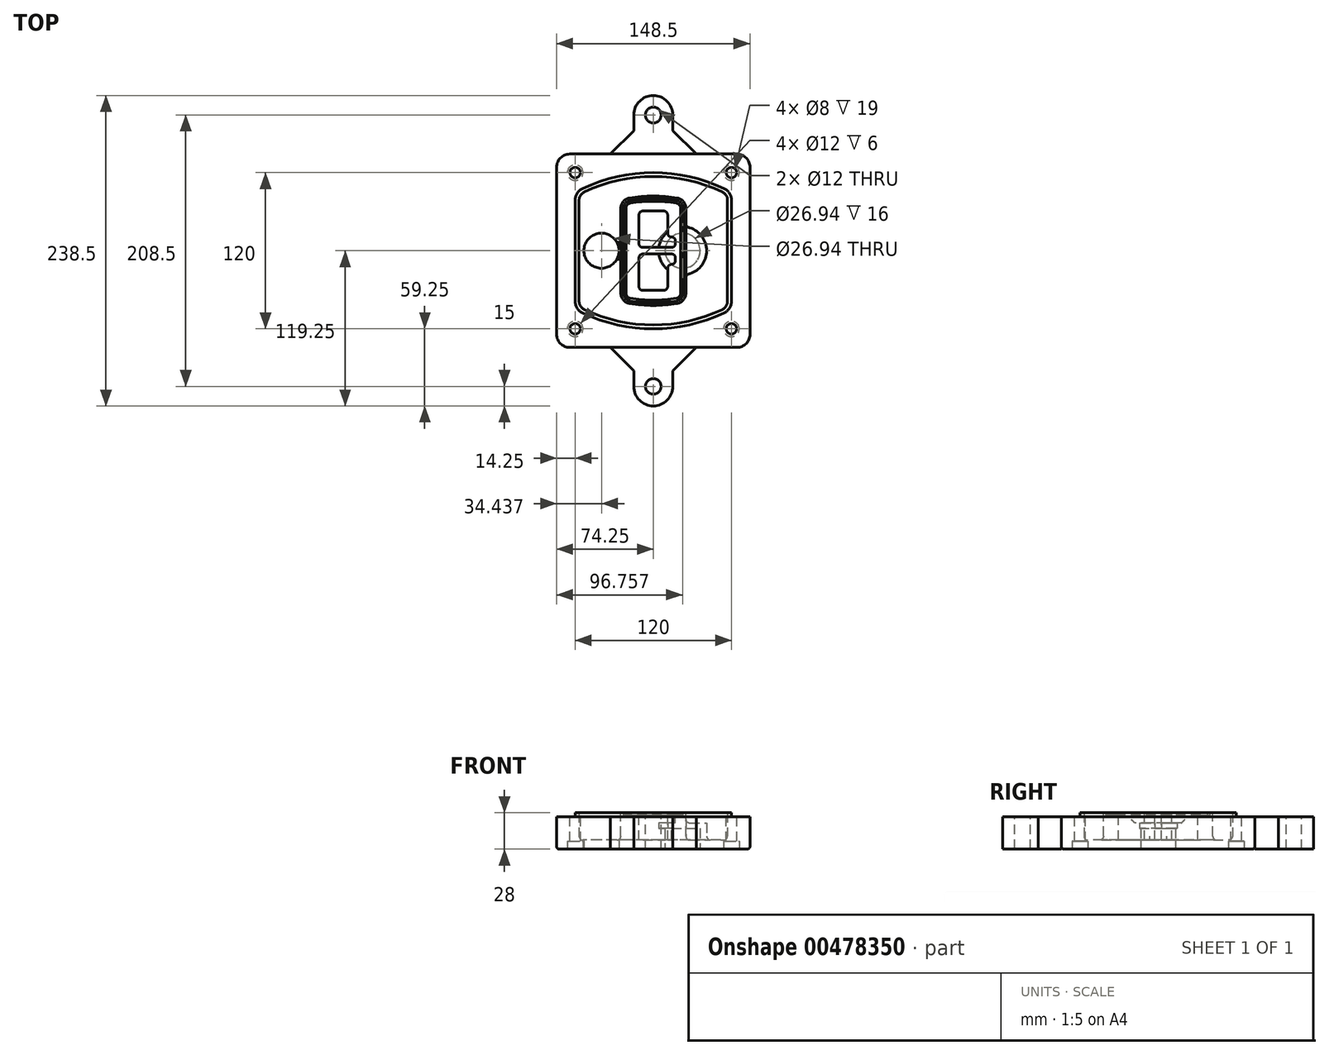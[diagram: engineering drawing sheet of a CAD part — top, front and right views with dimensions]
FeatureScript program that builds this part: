
annotation { "Feature Type Name" : "Feature", "Feature Type Description" : "" }
export const myFeature = defineFeature(function(context is Context, id is Id, definition is map)
    precondition{}
    {
        {
            var Q0;
            Q0=qCreatedBy(makeId("Top.planeOp"),FACE);
            var sketch = newSketch(context, id + "F0", { "sketchPlane" : qUnion([Q0])});
            skPoint(sketch, "E0.rect.middle", {"position": v(0, 0) * mm});
            skLineSegment(sketch, "E1.bottom", {"start": v(-64.25, -74.25) * mm, "end": v(64.25, -74.25) * mm});
            skLineSegment(sketch, "E1.top", {"start": v(-64.25, 74.25) * mm, "end": v(64.25, 74.25) * mm});
            skLineSegment(sketch, "E1.left", {"start": v(-74.25, -64.25) * mm, "end": v(-74.25, 64.25) * mm});
            skLineSegment(sketch, "E1.right", {"start": v(74.25, -64.25) * mm, "end": v(74.25, 64.25) * mm});
            skLineSegment(sketch, "E2", {"start": v(-74.25, 74.25) * mm, "end": v(74.25, -74.25) * mm, "construction": true});
            skLineSegment(sketch, "E3", {"start": v(74.25, 74.25) * mm, "end": v(-74.25, -74.25) * mm, "construction": true});
            skCircle(sketch, "E4", {"center": v(-60, 60) * mm, "radius": 4 * mm});
            skCircle(sketch, "E5", {"center": v(60, 60) * mm, "radius": 4 * mm});
            skCircle(sketch, "E6", {"center": v(60, -60) * mm, "radius": 4 * mm});
            skCircle(sketch, "E7", {"center": v(-60, -60) * mm, "radius": 4 * mm});
            skLineSegment(sketch, "E8", {"start": v(-60, 60) * mm, "end": v(60, 60) * mm, "construction": true});
            skLineSegment(sketch, "E9", {"start": v(60, 60) * mm, "end": v(60, -60) * mm, "construction": true});
            skLineSegment(sketch, "E10", {"start": v(60, -60) * mm, "end": v(-60, -60) * mm, "construction": true});
            skLineSegment(sketch, "E11", {"start": v(-60, -60) * mm, "end": v(-60, 60) * mm, "construction": true});
            skLineSegment(sketch, "E12", {"start": v(-60, 38.83) * mm, "end": v(-60, -38.83) * mm});
            skLineSegment(sketch, "E13", {"start": v(60, 38.83) * mm, "end": v(60, -38.83) * mm});
            skArc(sketch, "E14", {"start": v(54.26, 47.88) * mm, "mid": v(0, 60) * mm, "end": v(-54.26, 47.88) * mm});
            skArc(sketch, "E15", {"start": v(-54.26, -47.88) * mm, "mid": v(0, -60) * mm, "end": v(54.26, -47.88) * mm});
            skLineSegment(sketch, "E16", {"start": v(-60, 0) * mm, "end": v(60, 0) * mm, "construction": true});
            skPoint(sketch, "E17.visualSharp", {"position": v(-60, -45) * mm});
            skArc(sketch, "E17.filletArc", {"start": v(-60, -38.83) * mm, "mid": v(-58.44, -44.2) * mm, "end": v(-54.26, -47.88) * mm});
            skPoint(sketch, "E18.visualSharp", {"position": v(-60, 45) * mm});
            skArc(sketch, "E18.filletArc", {"start": v(-54.26, 47.88) * mm, "mid": v(-58.44, 44.2) * mm, "end": v(-60, 38.83) * mm});
            skPoint(sketch, "E19.visualSharp", {"position": v(60, 45) * mm});
            skArc(sketch, "E19.filletArc", {"start": v(60, 38.83) * mm, "mid": v(58.44, 44.2) * mm, "end": v(54.26, 47.88) * mm});
            skPoint(sketch, "E20.visualSharp", {"position": v(60, -45) * mm});
            skArc(sketch, "E20.filletArc", {"start": v(54.26, -47.88) * mm, "mid": v(58.44, -44.2) * mm, "end": v(60, -38.83) * mm});
            skPoint(sketch, "E21.visualSharp", {"position": v(-74.25, 74.25) * mm});
            skArc(sketch, "E21.filletArc", {"start": v(-64.25, 74.25) * mm, "mid": v(-71.32, 71.32) * mm, "end": v(-74.25, 64.25) * mm});
            skPoint(sketch, "E22.visualSharp", {"position": v(74.25, 74.25) * mm});
            skArc(sketch, "E22.filletArc", {"start": v(74.25, 64.25) * mm, "mid": v(71.32, 71.32) * mm, "end": v(64.25, 74.25) * mm});
            skPoint(sketch, "E23.visualSharp", {"position": v(74.25, -74.25) * mm});
            skArc(sketch, "E23.filletArc", {"start": v(64.25, -74.25) * mm, "mid": v(71.32, -71.32) * mm, "end": v(74.25, -64.25) * mm});
            skPoint(sketch, "E24.visualSharp", {"position": v(-74.25, -74.25) * mm});
            skArc(sketch, "E24.filletArc", {"start": v(-74.25, -64.25) * mm, "mid": v(-71.32, -71.32) * mm, "end": v(-64.25, -74.25) * mm});
            skArc(sketch, "E25.0", {"start": v(57, 38.83) * mm, "mid": v(55.9, 42.58) * mm, "end": v(52.98, 45.17) * mm});
            skLineSegment(sketch, "E25.1", {"start": v(57, 38.83) * mm, "end": v(57, -38.83) * mm});
            skArc(sketch, "E25.2", {"start": v(52.98, -45.17) * mm, "mid": v(55.9, -42.58) * mm, "end": v(57, -38.83) * mm});
            skArc(sketch, "E25.3", {"start": v(-52.98, -45.17) * mm, "mid": v(0, -57) * mm, "end": v(52.98, -45.17) * mm});
            skArc(sketch, "E25.4", {"start": v(-57, -38.83) * mm, "mid": v(-55.9, -42.58) * mm, "end": v(-52.98, -45.17) * mm});
            skArc(sketch, "E25.5", {"start": v(52.98, 45.17) * mm, "mid": v(0, 57) * mm, "end": v(-52.98, 45.17) * mm});
            skLineSegment(sketch, "E25.6", {"start": v(-57, 38.83) * mm, "end": v(-57, -38.83) * mm});
            skArc(sketch, "E25.7", {"start": v(-52.98, 45.17) * mm, "mid": v(-55.9, 42.58) * mm, "end": v(-57, 38.83) * mm});
            skArc(sketch, "E26.0", {"start": v(-55.96, 51.5) * mm, "mid": v(-61.82, 46.33) * mm, "end": v(-64, 38.83) * mm});
            skArc(sketch, "E26.1", {"start": v(55.96, 51.5) * mm, "mid": v(0, 64) * mm, "end": v(-55.96, 51.5) * mm});
            skArc(sketch, "E26.2", {"start": v(64, 38.83) * mm, "mid": v(61.82, 46.33) * mm, "end": v(55.96, 51.5) * mm});
            skLineSegment(sketch, "E26.3", {"start": v(64, 38.83) * mm, "end": v(64, -38.83) * mm});
            skArc(sketch, "E26.4", {"start": v(55.96, -51.5) * mm, "mid": v(61.82, -46.33) * mm, "end": v(64, -38.83) * mm});
            skLineSegment(sketch, "E26.5", {"start": v(-64, 38.83) * mm, "end": v(-64, -38.83) * mm});
            skArc(sketch, "E26.6", {"start": v(-55.96, -51.5) * mm, "mid": v(0, -64) * mm, "end": v(55.96, -51.5) * mm});
            skArc(sketch, "E26.7", {"start": v(-64, -38.83) * mm, "mid": v(-61.82, -46.33) * mm, "end": v(-55.96, -51.5) * mm});
            skSolve(sketch);
        }
        {
            var Q0;
            Q0=makeQuery(id+"F0.imprint","IMPRINT",FACE,{"disambiguationData":[TD([[makeQuery(id+"F0.imprint","IMPRINT",EDGE,{"derivedFrom":sQuery(id+"F0.wireOp",EDGE,"E1.bottom")}),1.0]])]});
            var Q1;
            Q1=makeQuery(id+"F0.imprint","IMPRINT",FACE,{"disambiguationData":[TD([[makeQuery(id+"F0.imprint","IMPRINT",EDGE,{"derivedFrom":sQuery(id+"F0.wireOp",EDGE,"E12")}),1.0]])]});
            var Q2;
            Q2=makeQuery(id+"F0.imprint","IMPRINT",FACE,{"disambiguationData":[TD([[makeQuery(id+"F0.imprint","IMPRINT",EDGE,{"derivedFrom":sQuery(id+"F0.wireOp",EDGE,"E25.0")}),1.0]])]});
            var Q3;
            Q3=makeQuery(id+"F0.imprint","IMPRINT",FACE,{"disambiguationData":[TD([[makeQuery(id+"F0.imprint","IMPRINT",EDGE,{"derivedFrom":sQuery(id+"F0.wireOp",EDGE,"E12")}),-1.0]])]});
            extrude(context, id + "F1", {"entities" : qUnion([Q0, Q1, Q2, Q3]), "oppositeDirection" : true, "depth" : 25 * mm});
        }
        {
            var Q0;
            Q0=makeQuery(id+"F0.imprint","IMPRINT",FACE,{"disambiguationData":[TD([[makeQuery(id+"F0.imprint","IMPRINT",EDGE,{"derivedFrom":sQuery(id+"F0.wireOp",EDGE,"E12")}),1.0]])]});
            extrude(context, id + "F2", {"entities" : qUnion([Q0]), "operationType" : NewBodyOperationType.ADD, "depth" : 3 * mm});
        }
        {
            var Q0;
            Q0=makeQuery(id+"F0.imprint","IMPRINT",FACE,{"disambiguationData":[TD([[makeQuery(id+"F0.imprint","IMPRINT",EDGE,{"derivedFrom":sQuery(id+"F0.wireOp",EDGE,"E25.0")}),1.0]])]});
            extrude(context, id + "F3", {"entities" : qUnion([Q0]), "operationType" : NewBodyOperationType.REMOVE, "oppositeDirection" : true, "depth" : 18 * mm});
        }
        {
            var Q0;
            Q0=makeQuery(id+"F2.opExtrude","CAP_FACE",FACE,{"disambiguationData":[OSD([sQuery(id+"F0.wireOp",EDGE,"E12"),sQuery(id+"F0.wireOp",EDGE,"E13"),sQuery(id+"F0.wireOp",EDGE,"E14"),sQuery(id+"F0.wireOp",EDGE,"E15"),sQuery(id+"F0.wireOp",EDGE,"E17.filletArc"),sQuery(id+"F0.wireOp",EDGE,"E18.filletArc"),sQuery(id+"F0.wireOp",EDGE,"E19.filletArc"),sQuery(id+"F0.wireOp",EDGE,"E20.filletArc"),sQuery(id+"F0.wireOp",EDGE,"E25.0"),sQuery(id+"F0.wireOp",EDGE,"E25.1"),sQuery(id+"F0.wireOp",EDGE,"E25.2"),sQuery(id+"F0.wireOp",EDGE,"E25.3"),sQuery(id+"F0.wireOp",EDGE,"E25.4"),sQuery(id+"F0.wireOp",EDGE,"E25.5"),sQuery(id+"F0.wireOp",EDGE,"E25.6"),sQuery(id+"F0.wireOp",EDGE,"E25.7")])],"isStart":false});
            var sketch = newSketch(context, id + "F4", { "sketchPlane" : qUnion([Q0])});
            skArc(sketch, "E27.0", {"start": v(-18.34, -40.45) * mm, "mid": v(0, -42) * mm, "end": v(18.34, -40.45) * mm});
            skArc(sketch, "E28.0", {"start": v(18.34, 40.45) * mm, "mid": v(0, 42) * mm, "end": v(-18.34, 40.45) * mm});
            skLineSegment(sketch, "E29", {"start": v(-25, 32.57) * mm, "end": v(-25, -32.57) * mm});
            skLineSegment(sketch, "E30", {"start": v(25, 32.57) * mm, "end": v(25, -32.57) * mm});
            skLineSegment(sketch, "E31", {"start": v(-25, 39.1) * mm, "end": v(25, 39.1) * mm, "construction": true});
            skLineSegment(sketch, "E32", {"start": v(-25, -39.1) * mm, "end": v(25, -39.1) * mm, "construction": true});
            skPoint(sketch, "E33.visualSharp", {"position": v(-25, 39.1) * mm});
            skArc(sketch, "E33.filletArc", {"start": v(-18.34, 40.45) * mm, "mid": v(-23.11, 37.73) * mm, "end": v(-25, 32.57) * mm});
            skPoint(sketch, "E34.visualSharp", {"position": v(25, 39.1) * mm});
            skArc(sketch, "E34.filletArc", {"start": v(25, 32.57) * mm, "mid": v(23.11, 37.73) * mm, "end": v(18.34, 40.45) * mm});
            skPoint(sketch, "E35.visualSharp", {"position": v(25, -39.1) * mm});
            skArc(sketch, "E35.filletArc", {"start": v(18.34, -40.45) * mm, "mid": v(23.11, -37.73) * mm, "end": v(25, -32.57) * mm});
            skPoint(sketch, "E36.visualSharp", {"position": v(-25, -39.1) * mm});
            skArc(sketch, "E36.filletArc", {"start": v(-25, -32.57) * mm, "mid": v(-23.11, -37.73) * mm, "end": v(-18.34, -40.45) * mm});
            skArc(sketch, "E37.0", {"start": v(52.98, 45.17) * mm, "mid": v(0, 57) * mm, "end": v(-52.98, 45.17) * mm});
            skArc(sketch, "E37.1", {"start": v(-52.98, 45.17) * mm, "mid": v(-55.9, 42.58) * mm, "end": v(-57, 38.83) * mm});
            skLineSegment(sketch, "E37.2", {"start": v(-57, 38.83) * mm, "end": v(-57, -38.83) * mm});
            skArc(sketch, "E37.3", {"start": v(-57, -38.83) * mm, "mid": v(-55.9, -42.58) * mm, "end": v(-52.98, -45.17) * mm});
            skArc(sketch, "E37.4", {"start": v(-52.98, -45.17) * mm, "mid": v(0, -57) * mm, "end": v(52.98, -45.17) * mm});
            skArc(sketch, "E37.5", {"start": v(52.98, -45.17) * mm, "mid": v(55.9, -42.58) * mm, "end": v(57, -38.83) * mm});
            skLineSegment(sketch, "E37.6", {"start": v(57, 38.83) * mm, "end": v(57, -38.83) * mm});
            skArc(sketch, "E37.7", {"start": v(57, 38.83) * mm, "mid": v(55.9, 42.58) * mm, "end": v(52.98, 45.17) * mm});
            skLineSegment(sketch, "E38.0", {"start": v(23, 32.57) * mm, "end": v(23, -32.57) * mm});
            skArc(sketch, "E38.1", {"start": v(18, -38.48) * mm, "mid": v(21.58, -36.44) * mm, "end": v(23, -32.57) * mm});
            skArc(sketch, "E38.2", {"start": v(-18, -38.48) * mm, "mid": v(0, -40) * mm, "end": v(18, -38.48) * mm});
            skArc(sketch, "E38.3", {"start": v(-23, -32.57) * mm, "mid": v(-21.58, -36.44) * mm, "end": v(-18, -38.48) * mm});
            skLineSegment(sketch, "E38.4", {"start": v(-23, 32.57) * mm, "end": v(-23, -32.57) * mm});
            skArc(sketch, "E38.5", {"start": v(23, 32.57) * mm, "mid": v(21.58, 36.44) * mm, "end": v(18, 38.48) * mm});
            skArc(sketch, "E38.6", {"start": v(-18, 38.48) * mm, "mid": v(-21.58, 36.44) * mm, "end": v(-23, 32.57) * mm});
            skArc(sketch, "E38.7", {"start": v(18, 38.48) * mm, "mid": v(0, 40) * mm, "end": v(-18, 38.48) * mm});
            skArc(sketch, "E39.0", {"start": v(21, 32.57) * mm, "mid": v(20.06, 35.15) * mm, "end": v(17.67, 36.5) * mm});
            skLineSegment(sketch, "E39.1", {"start": v(21, 32.57) * mm, "end": v(21, -32.57) * mm});
            skArc(sketch, "E39.2", {"start": v(17.67, -36.5) * mm, "mid": v(20.06, -35.15) * mm, "end": v(21, -32.57) * mm});
            skArc(sketch, "E39.3", {"start": v(-17.67, -36.5) * mm, "mid": v(0, -38) * mm, "end": v(17.67, -36.5) * mm});
            skArc(sketch, "E39.4", {"start": v(-21, -32.57) * mm, "mid": v(-20.06, -35.15) * mm, "end": v(-17.67, -36.5) * mm});
            skArc(sketch, "E39.5", {"start": v(17.67, 36.5) * mm, "mid": v(0, 38) * mm, "end": v(-17.67, 36.5) * mm});
            skLineSegment(sketch, "E39.6", {"start": v(-21, 32.57) * mm, "end": v(-21, -32.57) * mm});
            skArc(sketch, "E39.7", {"start": v(-17.67, 36.5) * mm, "mid": v(-20.06, 35.15) * mm, "end": v(-21, 32.57) * mm});
            skLineSegment(sketch, "E40", {"start": v(-25, 0) * mm, "end": v(25, 0) * mm, "construction": true});
            skLineSegment(sketch, "E41", {"start": v(-11, 5.5) * mm, "end": v(-11, 27.5) * mm});
            skLineSegment(sketch, "E42", {"start": v(-8, 30.5) * mm, "end": v(8, 30.5) * mm});
            skLineSegment(sketch, "E43", {"start": v(11, 27.5) * mm, "end": v(11, 13.5) * mm});
            skLineSegment(sketch, "E44", {"start": v(14, 10.5) * mm, "end": v(14, 10.5) * mm});
            skLineSegment(sketch, "E45", {"start": v(17, 7.5) * mm, "end": v(17, 5.5) * mm});
            skLineSegment(sketch, "E46", {"start": v(14, 2.5) * mm, "end": v(-8, 2.5) * mm});
            skPoint(sketch, "E47.visualSharp", {"position": v(-11, 30.5) * mm});
            skArc(sketch, "E47.filletArc", {"start": v(-8, 30.5) * mm, "mid": v(-10.12, 29.62) * mm, "end": v(-11, 27.5) * mm});
            skPoint(sketch, "E48.visualSharp", {"position": v(11, 30.5) * mm});
            skArc(sketch, "E48.filletArc", {"start": v(11, 27.5) * mm, "mid": v(10.12, 29.62) * mm, "end": v(8, 30.5) * mm});
            skPoint(sketch, "E49.visualSharp", {"position": v(11, 10.5) * mm});
            skArc(sketch, "E49.filletArc", {"start": v(11, 13.5) * mm, "mid": v(11.88, 11.38) * mm, "end": v(14, 10.5) * mm});
            skPoint(sketch, "E50.visualSharp", {"position": v(17, 10.5) * mm});
            skArc(sketch, "E50.filletArc", {"start": v(17, 7.5) * mm, "mid": v(16.12, 9.62) * mm, "end": v(14, 10.5) * mm});
            skPoint(sketch, "E51.visualSharp", {"position": v(17, 2.5) * mm});
            skArc(sketch, "E51.filletArc", {"start": v(14, 2.5) * mm, "mid": v(16.12, 3.38) * mm, "end": v(17, 5.5) * mm});
            skPoint(sketch, "E52.visualSharp", {"position": v(-11, 2.5) * mm});
            skArc(sketch, "E52.filletArc", {"start": v(-11, 5.5) * mm, "mid": v(-10.12, 3.38) * mm, "end": v(-8, 2.5) * mm});
            skLineSegment(sketch, "E53.0.MirrorCS", {"start": v(14, -2.5) * mm, "end": v(-8, -2.5) * mm});
            skArc(sketch, "E54.0.MirrorCS", {"start": v(-11, -5.5) * mm, "mid": v(-10.12, -3.38) * mm, "end": v(-8, -2.5) * mm});
            skLineSegment(sketch, "E55.0.MirrorCS", {"start": v(-11, -5.5) * mm, "end": v(-11, -27.5) * mm});
            skArc(sketch, "E56.0.MirrorCS", {"start": v(-8, -30.5) * mm, "mid": v(-10.12, -29.62) * mm, "end": v(-11, -27.5) * mm});
            skLineSegment(sketch, "E57.0.MirrorCS", {"start": v(-8, -30.5) * mm, "end": v(8, -30.5) * mm});
            skArc(sketch, "E58.0.MirrorCS", {"start": v(11, -27.5) * mm, "mid": v(10.12, -29.62) * mm, "end": v(8, -30.5) * mm});
            skLineSegment(sketch, "E59.0.MirrorCS", {"start": v(11, -27.5) * mm, "end": v(11, -13.5) * mm});
            skArc(sketch, "E60.0.MirrorCS", {"start": v(11, -13.5) * mm, "mid": v(11.88, -11.38) * mm, "end": v(14, -10.5) * mm});
            skArc(sketch, "E61.0.MirrorCS", {"start": v(17, -7.5) * mm, "mid": v(16.12, -9.62) * mm, "end": v(14, -10.5) * mm});
            skLineSegment(sketch, "E62.0.MirrorCS", {"start": v(17, -7.5) * mm, "end": v(17, -5.5) * mm});
            skArc(sketch, "E63.0.MirrorCS", {"start": v(14, -2.5) * mm, "mid": v(16.12, -3.38) * mm, "end": v(17, -5.5) * mm});
            skSolve(sketch);
        }
        {
            var Q0;
            Q0=makeQuery(id+"F4.imprint","IMPRINT",FACE,{"disambiguationData":[TD([[makeQuery(id+"F4.imprint","IMPRINT",EDGE,{"derivedFrom":sQuery(id+"F4.wireOp",EDGE,"E27.0")}),1.0]])]});
            var Q1;
            Q1=makeQuery(id+"F4.imprint","IMPRINT",FACE,{"disambiguationData":[TD([[makeQuery(id+"F4.imprint","IMPRINT",EDGE,{"derivedFrom":sQuery(id+"F4.wireOp",EDGE,"E38.0")}),-1.0]])]});
            var Q2;
            Q2=makeQuery(id+"F4.imprint","IMPRINT",FACE,{"disambiguationData":[TD([[makeQuery(id+"F4.imprint","IMPRINT",EDGE,{"derivedFrom":sQuery(id+"F4.wireOp",EDGE,"E39.0")}),1.0]])]});
            extrude(context, id + "F5", {"entities" : qUnion([Q0, Q1, Q2]), "operationType" : NewBodyOperationType.ADD, "endBound" : BoundingType.UP_TO_NEXT, "oppositeDirection" : true, "depth" : 25 * mm});
        }
        {
            var Q0;
            Q0=makeQuery(id+"F4.imprint","IMPRINT",FACE,{"disambiguationData":[TD([[makeQuery(id+"F4.imprint","IMPRINT",EDGE,{"derivedFrom":sQuery(id+"F4.wireOp",EDGE,"E38.0")}),-1.0]])]});
            extrude(context, id + "F6", {"entities" : qUnion([Q0]), "operationType" : NewBodyOperationType.REMOVE, "oppositeDirection" : true, "depth" : 2 * mm});
        }
        {
            var Q0;
            Q0=makeQuery(id+"F1.opExtrude","CAP_FACE",FACE,{"disambiguationData":[OSD([sQuery(id+"F0.wireOp",EDGE,"E1.bottom"),sQuery(id+"F0.wireOp",EDGE,"E1.top"),sQuery(id+"F0.wireOp",EDGE,"E1.left"),sQuery(id+"F0.wireOp",EDGE,"E1.right"),sQuery(id+"F0.wireOp",EDGE,"E4"),sQuery(id+"F0.wireOp",EDGE,"E5"),sQuery(id+"F0.wireOp",EDGE,"E6"),sQuery(id+"F0.wireOp",EDGE,"E7"),sQuery(id+"F0.wireOp",EDGE,"E21.filletArc"),sQuery(id+"F0.wireOp",EDGE,"E22.filletArc"),sQuery(id+"F0.wireOp",EDGE,"E23.filletArc"),sQuery(id+"F0.wireOp",EDGE,"E24.filletArc")])],"isStart":false});
            var sketch = newSketch(context, id + "F7", { "sketchPlane" : qUnion([Q0])});
            skCircle(sketch, "E64", {"center": v(22.5, 0) * mm, "radius": 13.47 * mm});
            skCircle(sketch, "E65", {"center": v(-39.81, 0) * mm, "radius": 13.47 * mm});
            skLineSegment(sketch, "E66", {"start": v(74.25, 0) * mm, "end": v(-74.25, 0) * mm});
            skCircle(sketch, "E67", {"center": v(22.5, 0) * mm, "radius": 18.47 * mm});
            skCircle(sketch, "E68", {"center": v(60, -60) * mm, "radius": 6 * mm});
            skCircle(sketch, "E69", {"center": v(-60, -60) * mm, "radius": 6 * mm});
            skCircle(sketch, "E70", {"center": v(-60, 60) * mm, "radius": 6 * mm});
            skCircle(sketch, "E71", {"center": v(60, 60) * mm, "radius": 6 * mm});
            skSolve(sketch);
        }
        {
            var Q0;
            {var subQ1=sQuery(id+"F7.wireOp",EDGE,"E66");var subQ4=sQuery(id+"F7.wireOp",EDGE,"E64");var subQ6=makeQuery(id+"F7.imprint","INTERSECT",VERTEX,{"disambiguationData":[OD(0.0)],"derivedFrom":[subQ4,subQ1]});Q0=makeQuery(id+"F7.imprint","IMPRINT",FACE,{"disambiguationData":[TD([[makeQuery(id+"F7.imprint","IMPRINT",EDGE,{"disambiguationData":[TD([[subQ6,-1.0]])],"derivedFrom":subQ4}),-1.0]])]});}
            var Q1;
            {var subQ0=sQuery(id+"F7.wireOp",EDGE,"E66");var subQ1=sQuery(id+"F7.wireOp",EDGE,"E64");var subQ3=makeQuery(id+"F7.imprint","INTERSECT",VERTEX,{"disambiguationData":[OD(0.0)],"derivedFrom":[subQ1,subQ0]});Q1=makeQuery(id+"F7.imprint","IMPRINT",FACE,{"disambiguationData":[TD([[makeQuery(id+"F7.imprint","IMPRINT",EDGE,{"disambiguationData":[TD([[subQ3,-1.0]])],"derivedFrom":subQ1}),1.0]])]});}
            var Q2;
            {var subQ0=sQuery(id+"F7.wireOp",EDGE,"E66");var subQ1=sQuery(id+"F7.wireOp",EDGE,"E64");var subQ3=makeQuery(id+"F7.imprint","INTERSECT",VERTEX,{"disambiguationData":[OD(0.0)],"derivedFrom":[subQ1,subQ0]});Q2=makeQuery(id+"F7.imprint","IMPRINT",FACE,{"disambiguationData":[TD([[makeQuery(id+"F7.imprint","IMPRINT",EDGE,{"disambiguationData":[TD([[subQ3,1.0]])],"derivedFrom":subQ1}),1.0]])]});}
            var Q3;
            {var subQ1=sQuery(id+"F7.wireOp",EDGE,"E66");var subQ4=sQuery(id+"F7.wireOp",EDGE,"E64");var subQ6=makeQuery(id+"F7.imprint","INTERSECT",VERTEX,{"disambiguationData":[OD(0.0)],"derivedFrom":[subQ4,subQ1]});Q3=makeQuery(id+"F7.imprint","IMPRINT",FACE,{"disambiguationData":[TD([[makeQuery(id+"F7.imprint","IMPRINT",EDGE,{"disambiguationData":[TD([[subQ6,1.0]])],"derivedFrom":subQ4}),-1.0]])]});}
            extrude(context, id + "F8", {"entities" : qUnion([Q0, Q1, Q2, Q3]), "operationType" : NewBodyOperationType.ADD, "oppositeDirection" : true, "depth" : 20 * mm});
        }
        {
            var Q0;
            {var subQ0=sQuery(id+"F7.wireOp",EDGE,"E66");var subQ1=sQuery(id+"F7.wireOp",EDGE,"E64");var subQ3=makeQuery(id+"F7.imprint","INTERSECT",VERTEX,{"disambiguationData":[OD(0.0)],"derivedFrom":[subQ1,subQ0]});Q0=makeQuery(id+"F7.imprint","IMPRINT",FACE,{"disambiguationData":[TD([[makeQuery(id+"F7.imprint","IMPRINT",EDGE,{"disambiguationData":[TD([[subQ3,-1.0]])],"derivedFrom":subQ1}),1.0]])]});}
            var Q1;
            {var subQ0=sQuery(id+"F7.wireOp",EDGE,"E66");var subQ1=sQuery(id+"F7.wireOp",EDGE,"E64");var subQ3=makeQuery(id+"F7.imprint","INTERSECT",VERTEX,{"disambiguationData":[OD(0.0)],"derivedFrom":[subQ1,subQ0]});Q1=makeQuery(id+"F7.imprint","IMPRINT",FACE,{"disambiguationData":[TD([[makeQuery(id+"F7.imprint","IMPRINT",EDGE,{"disambiguationData":[TD([[subQ3,1.0]])],"derivedFrom":subQ1}),1.0]])]});}
            extrude(context, id + "F9", {"entities" : qUnion([Q0, Q1]), "operationType" : NewBodyOperationType.REMOVE, "oppositeDirection" : true, "depth" : 16 * mm});
        }
        {
            var Q0;
            {var subQ0=sQuery(id+"F7.wireOp",EDGE,"E66");var subQ1=sQuery(id+"F7.wireOp",EDGE,"E65");var subQ3=makeQuery(id+"F7.imprint","INTERSECT",VERTEX,{"disambiguationData":[OD(0.0)],"derivedFrom":[subQ1,subQ0]});Q0=makeQuery(id+"F7.imprint","IMPRINT",FACE,{"disambiguationData":[TD([[makeQuery(id+"F7.imprint","IMPRINT",EDGE,{"disambiguationData":[TD([[subQ3,-1.0]])],"derivedFrom":subQ1}),1.0]])]});}
            var Q1;
            {var subQ0=sQuery(id+"F7.wireOp",EDGE,"E66");var subQ1=sQuery(id+"F7.wireOp",EDGE,"E65");var subQ3=makeQuery(id+"F7.imprint","INTERSECT",VERTEX,{"disambiguationData":[OD(0.0)],"derivedFrom":[subQ1,subQ0]});Q1=makeQuery(id+"F7.imprint","IMPRINT",FACE,{"disambiguationData":[TD([[makeQuery(id+"F7.imprint","IMPRINT",EDGE,{"disambiguationData":[TD([[subQ3,1.0]])],"derivedFrom":subQ1}),1.0]])]});}
            extrude(context, id + "F10", {"entities" : qUnion([Q0, Q1]), "operationType" : NewBodyOperationType.REMOVE, "oppositeDirection" : true, "depth" : 25 * mm});
        }
        {
            var Q0;
            Q0=makeQuery(id+"F7.imprint","IMPRINT",FACE,{"disambiguationData":[TD([[makeQuery(id+"F7.imprint","IMPRINT",EDGE,{"derivedFrom":sQuery(id+"F7.wireOp",EDGE,"E68")}),1.0]])]});
            var Q1;
            Q1=makeQuery(id+"F7.imprint","IMPRINT",FACE,{"disambiguationData":[TD([[makeQuery(id+"F7.imprint","IMPRINT",EDGE,{"derivedFrom":makeQuery(id+"F1.opExtrude","CAP_EDGE",EDGE,{"disambiguationData":[OSD([sQuery(id+"F0.wireOp",EDGE,"E5")])],"isStart":false})}),-1.0]])]});
            var Q2;
            Q2=makeQuery(id+"F7.imprint","IMPRINT",FACE,{"disambiguationData":[TD([[makeQuery(id+"F7.imprint","IMPRINT",EDGE,{"derivedFrom":sQuery(id+"F7.wireOp",EDGE,"E69")}),1.0]])]});
            var Q3;
            Q3=makeQuery(id+"F7.imprint","IMPRINT",FACE,{"disambiguationData":[TD([[makeQuery(id+"F7.imprint","IMPRINT",EDGE,{"derivedFrom":makeQuery(id+"F1.opExtrude","CAP_EDGE",EDGE,{"disambiguationData":[OSD([sQuery(id+"F0.wireOp",EDGE,"E4")])],"isStart":false})}),-1.0]])]});
            var Q4;
            Q4=makeQuery(id+"F7.imprint","IMPRINT",FACE,{"disambiguationData":[TD([[makeQuery(id+"F7.imprint","IMPRINT",EDGE,{"derivedFrom":sQuery(id+"F7.wireOp",EDGE,"E70")}),1.0]])]});
            var Q5;
            Q5=makeQuery(id+"F7.imprint","IMPRINT",FACE,{"disambiguationData":[TD([[makeQuery(id+"F7.imprint","IMPRINT",EDGE,{"derivedFrom":makeQuery(id+"F1.opExtrude","CAP_EDGE",EDGE,{"disambiguationData":[OSD([sQuery(id+"F0.wireOp",EDGE,"E7")])],"isStart":false})}),-1.0]])]});
            var Q6;
            Q6=makeQuery(id+"F7.imprint","IMPRINT",FACE,{"disambiguationData":[TD([[makeQuery(id+"F7.imprint","IMPRINT",EDGE,{"derivedFrom":sQuery(id+"F7.wireOp",EDGE,"E71")}),1.0]])]});
            var Q7;
            Q7=makeQuery(id+"F7.imprint","IMPRINT",FACE,{"disambiguationData":[TD([[makeQuery(id+"F7.imprint","IMPRINT",EDGE,{"derivedFrom":makeQuery(id+"F1.opExtrude","CAP_EDGE",EDGE,{"disambiguationData":[OSD([sQuery(id+"F0.wireOp",EDGE,"E6")])],"isStart":false})}),-1.0]])]});
            extrude(context, id + "F11", {"entities" : qUnion([Q0, Q1, Q2, Q3, Q4, Q5, Q6, Q7]), "operationType" : NewBodyOperationType.REMOVE, "oppositeDirection" : true, "depth" : 6 * mm});
        }
        {
            var Q0;
            Q0=makeQuery(id+"F9.boolean.opBoolean","COPY",FACE,{"derivedFrom":makeQuery(id+"F9.opExtrude","CAP_FACE",FACE,{"disambiguationData":[OSD([sQuery(id+"F7.wireOp",EDGE,"E64")])],"isStart":false})});
            var sketch = newSketch(context, id + "F12", { "sketchPlane" : qUnion([Q0])});
            skArc(sketch, "E72.0", {"start": v(11, 14.45) * mm, "mid": v(6.45, 9.13) * mm, "end": v(4.2, 2.5) * mm});
            skArc(sketch, "E72.1", {"start": v(4.2, -2.5) * mm, "mid": v(6.45, -9.13) * mm, "end": v(11, -14.45) * mm});
            skLineSegment(sketch, "E73", {"start": v(4.2, -2.5) * mm, "end": v(14, -2.5) * mm});
            skLineSegment(sketch, "E74.0", {"start": v(14, 2.5) * mm, "end": v(4.2, 2.5) * mm});
            skArc(sketch, "E74.1", {"start": v(14, 2.5) * mm, "mid": v(16.12, 3.38) * mm, "end": v(17, 5.5) * mm});
            skLineSegment(sketch, "E74.2", {"start": v(17, 7.5) * mm, "end": v(17, 5.5) * mm});
            skArc(sketch, "E74.3", {"start": v(17, 7.5) * mm, "mid": v(16.12, 9.62) * mm, "end": v(14, 10.5) * mm});
            skArc(sketch, "E74.4", {"start": v(11, 13.5) * mm, "mid": v(11.88, 11.38) * mm, "end": v(14, 10.5) * mm});
            skLineSegment(sketch, "E74.5", {"start": v(11, 14.45) * mm, "end": v(11, 13.5) * mm});
            skLineSegment(sketch, "E74.7", {"start": v(14, -2.5) * mm, "end": v(4.2, -2.5) * mm});
            skArc(sketch, "E74.8", {"start": v(14, -2.5) * mm, "mid": v(16.12, -3.38) * mm, "end": v(17, -5.5) * mm});
            skLineSegment(sketch, "E74.9", {"start": v(17, -7.5) * mm, "end": v(17, -5.5) * mm});
            skArc(sketch, "E74.10", {"start": v(17, -7.5) * mm, "mid": v(16.12, -9.62) * mm, "end": v(14, -10.5) * mm});
            skArc(sketch, "E74.11", {"start": v(11, -13.5) * mm, "mid": v(11.88, -11.38) * mm, "end": v(14, -10.5) * mm});
            skLineSegment(sketch, "E74.12", {"start": v(11, -14.45) * mm, "end": v(11, -13.5) * mm});
            skPoint(sketch, "E75.orphan", {"position": v(11, -27.5) * mm});
            skPoint(sketch, "E76.orphan", {"position": v(-8, -2.5) * mm});
            skPoint(sketch, "E77.orphan", {"position": v(-8, 2.5) * mm});
            skPoint(sketch, "E78.orphan", {"position": v(11, 27.5) * mm});
            skSolve(sketch);
        }
        {
            var Q0;
            {var subQ7=sQuery(id+"F12.wireOp",EDGE,"E72.0");var subQ14=sQuery(id+"F12.wireOp",EDGE,"E72.1");var subQ16=sQuery(id+"F12.wireOp",EDGE,"E74.1");var subQ18=sQuery(id+"F12.wireOp",EDGE,"E74.8");Q0=qUnion([makeQuery(id+"F12.imprint","IMPRINT",FACE,{"disambiguationData":[TD([[makeQuery(id+"F12.imprint","IMPRINT",EDGE,{"derivedFrom":subQ7}),1.0]])]}),makeQuery(id+"F12.imprint","IMPRINT",FACE,{"disambiguationData":[TD([[makeQuery(id+"F12.imprint","IMPRINT",EDGE,{"derivedFrom":subQ14}),1.0]])]}),makeQuery(id+"F12.imprint","IMPRINT",FACE,{"disambiguationData":[TD([[makeQuery(id+"F12.imprint","IMPRINT",EDGE,{"derivedFrom":subQ16}),1.0]])]}),makeQuery(id+"F12.imprint","IMPRINT",FACE,{"disambiguationData":[TD([[makeQuery(id+"F12.imprint","IMPRINT",EDGE,{"derivedFrom":subQ18}),-1.0]])]})]);}
            var Q1;
            Q1=makeQuery(id+"F5.boolean.opBoolean","SPLIT",FACE,{"disambiguationData":[TD([makeQuery(id+"F5.opExtrude","SWEPT_FACE",FACE,{"disambiguationData":[OSD([sQuery(id+"F4.wireOp",EDGE,"E41")])]})])],"derivedFrom":makeQuery(id+"F3.boolean.opBoolean","COPY",FACE,{"derivedFrom":makeQuery(id+"F3.opExtrude","CAP_FACE",FACE,{"disambiguationData":[OSD([sQuery(id+"F0.wireOp",EDGE,"E25.0"),sQuery(id+"F0.wireOp",EDGE,"E25.1"),sQuery(id+"F0.wireOp",EDGE,"E25.2"),sQuery(id+"F0.wireOp",EDGE,"E25.3"),sQuery(id+"F0.wireOp",EDGE,"E25.4"),sQuery(id+"F0.wireOp",EDGE,"E25.5"),sQuery(id+"F0.wireOp",EDGE,"E25.6"),sQuery(id+"F0.wireOp",EDGE,"E25.7")])],"isStart":false})})});
            extrude(context, id + "F13", {"entities" : qUnion([Q0]), "operationType" : NewBodyOperationType.REMOVE, "endBound" : BoundingType.UP_TO_SURFACE, "endBoundEntityFace" : qUnion([Q1]), "depth" : 25 * mm});
        }
        {
            var Q0;
            Q0=makeQuery(id+"F3.boolean.opBoolean","COPY",EDGE,{"derivedFrom":makeQuery(id+"F3.opExtrude","CAP_EDGE",EDGE,{"disambiguationData":[OSD([sQuery(id+"F0.wireOp",EDGE,"E25.6")])],"isStart":false})});
            var Q1;
            Q1=makeQuery(id+"F8.boolean.opBoolean","INTERSECT",EDGE,{"derivedFrom":[makeQuery(id+"F5.opExtrude","SWEPT_FACE",FACE,{"disambiguationData":[OSD([sQuery(id+"F4.wireOp",EDGE,"E30")])]}),makeQuery(id+"F8.opExtrude","CAP_FACE",FACE,{"disambiguationData":[OSD([sQuery(id+"F7.wireOp",EDGE,"E67")])],"isStart":false})]});
            var Q2;
            Q2=makeQuery(id+"F8.boolean.opBoolean","INTERSECT",EDGE,{"disambiguationData":[OD(1.0)],"derivedFrom":[makeQuery(id+"F5.opExtrude","SWEPT_FACE",FACE,{"disambiguationData":[OSD([sQuery(id+"F4.wireOp",EDGE,"E30")])]}),makeQuery(id+"F8.opExtrude","SWEPT_FACE",FACE,{"disambiguationData":[OSD([sQuery(id+"F7.wireOp",EDGE,"E67")])]})]});
            var Q3;
            {var subQ0=sQuery(id+"F4.wireOp",EDGE,"E30");Q3=makeQuery(id+"F8.boolean.opBoolean","SPLIT",EDGE,{"disambiguationData":[TD([makeQuery(id+"F5.opExtrude","SWEPT_FACE",FACE,{"disambiguationData":[OSD([sQuery(id+"F4.wireOp",EDGE,"E35.filletArc")])]})])],"derivedFrom":makeQuery(id+"F5.opExtrude","CAP_EDGE",EDGE,{"disambiguationData":[OSD([subQ0])],"isStart":false})});}
            var Q4;
            {var subQ0=sQuery(id+"F0.wireOp",EDGE,"E25.7");var subQ1=sQuery(id+"F0.wireOp",EDGE,"E25.1");var subQ2=sQuery(id+"F0.wireOp",EDGE,"E25.6");var subQ3=sQuery(id+"F0.wireOp",EDGE,"E25.5");var subQ4=sQuery(id+"F0.wireOp",EDGE,"E25.4");var subQ5=sQuery(id+"F0.wireOp",EDGE,"E25.0");var subQ6=sQuery(id+"F0.wireOp",EDGE,"E25.2");var subQ7=sQuery(id+"F0.wireOp",EDGE,"E25.3");Q4=makeQuery(id+"F8.boolean.opBoolean","INTERSECT",EDGE,{"derivedFrom":[makeQuery(id+"F5.boolean.opBoolean","SPLIT",FACE,{"disambiguationData":[TD([makeQuery(id+"F2.opExtrude","SWEPT_FACE",FACE,{"disambiguationData":[OSD([subQ5])]})])],"derivedFrom":makeQuery(id+"F3.boolean.opBoolean","COPY",FACE,{"derivedFrom":makeQuery(id+"F3.opExtrude","CAP_FACE",FACE,{"disambiguationData":[OSD([subQ5,subQ1,subQ6,subQ7,subQ4,subQ3,subQ2,subQ0])],"isStart":false})})}),makeQuery(id+"F8.opExtrude","SWEPT_FACE",FACE,{"disambiguationData":[OSD([sQuery(id+"F7.wireOp",EDGE,"E67")])]})]});}
            var Q5;
            Q5=makeQuery(id+"F8.boolean.opBoolean","INTERSECT",EDGE,{"disambiguationData":[OD(0.0)],"derivedFrom":[makeQuery(id+"F5.opExtrude","SWEPT_FACE",FACE,{"disambiguationData":[OSD([sQuery(id+"F4.wireOp",EDGE,"E30")])]}),makeQuery(id+"F8.opExtrude","SWEPT_FACE",FACE,{"disambiguationData":[OSD([sQuery(id+"F7.wireOp",EDGE,"E67")])]})]});
            fillet(context, id + "F14", {"entities" : qUnion([Q0, Q1, Q2, Q3, Q4, Q5]), "radius" : 3 * mm, "tangentPropagation" : true, "allowEdgeOverflow" : false});
        }
        {
            var Q0;
            Q0=makeQuery(id+"F1.opExtrude","CAP_EDGE",EDGE,{"disambiguationData":[OSD([sQuery(id+"F0.wireOp",EDGE,"E1.bottom")])],"isStart":false});
            fillet(context, id + "F15", {"entities" : qUnion([Q0]), "radius" : 2 * mm, "tangentPropagation" : true, "allowEdgeOverflow" : false});
        }
        {
            var Q0;
            {var subQ0=sQuery(id+"F0.wireOp",EDGE,"E21.filletArc");var subQ1=sQuery(id+"F0.wireOp",EDGE,"E7");var subQ2=sQuery(id+"F0.wireOp",EDGE,"E6");var subQ3=sQuery(id+"F0.wireOp",EDGE,"E5");var subQ4=sQuery(id+"F0.wireOp",EDGE,"E4");var subQ5=sQuery(id+"F0.wireOp",EDGE,"E22.filletArc");var subQ6=sQuery(id+"F0.wireOp",EDGE,"E1.bottom");var subQ7=sQuery(id+"F0.wireOp",EDGE,"E1.right");var subQ8=sQuery(id+"F0.wireOp",EDGE,"E1.top");var subQ9=sQuery(id+"F0.wireOp",EDGE,"E1.left");var subQ10=sQuery(id+"F0.wireOp",EDGE,"E23.filletArc");var subQ11=sQuery(id+"F0.wireOp",EDGE,"E24.filletArc");Q0=makeQuery(id+"F2.boolean.opBoolean","SPLIT",FACE,{"disambiguationData":[TD([makeQuery(id+"F1.opExtrude","SWEPT_FACE",FACE,{"disambiguationData":[OSD([subQ6])]})])],"derivedFrom":makeQuery(id+"F1.opExtrude","CAP_FACE",FACE,{"disambiguationData":[OSD([subQ6,subQ8,subQ9,subQ7,subQ4,subQ3,subQ2,subQ1,subQ0,subQ5,subQ10,subQ11])],"isStart":true})});}
            var sketch = newSketch(context, id + "F16", { "sketchPlane" : qUnion([Q0])});
            skSolve(sketch);
        }
        {
            var Q0;
            Q0=makeQuery(id+"F16.imprint","IMPRINT",FACE,{"disambiguationData":[TD([[makeQuery(id+"F16.imprint","IMPRINT",EDGE,{"derivedFrom":makeQuery(id+"F1.opExtrude","CAP_EDGE",EDGE,{"disambiguationData":[OSD([sQuery(id+"F0.wireOp",EDGE,"E1.bottom")])],"isStart":true})}),1.0]])]});
            var sketch = newSketch(context, id + "F17", { "sketchPlane" : qUnion([Q0])});
            skLineSegment(sketch, "E79", {"start": v(0, 74.25) * mm, "end": v(0, 104.25) * mm, "construction": true});
            skCircle(sketch, "E80", {"center": v(0, 104.25) * mm, "radius": 6 * mm});
            skLineSegment(sketch, "E81", {"start": v(33, 74.25) * mm, "end": v(-33, 74.25) * mm});
            skLineSegment(sketch, "E82", {"start": v(-33, 74.25) * mm, "end": v(-15, 92.25) * mm});
            skLineSegment(sketch, "E83", {"start": v(33, 74.25) * mm, "end": v(15, 92.25) * mm});
            skLineSegment(sketch, "E84", {"start": v(15, 92.25) * mm, "end": v(15, 104.25) * mm});
            skLineSegment(sketch, "E85", {"start": v(-15, 92.25) * mm, "end": v(-15, 104.25) * mm});
            skArc(sketch, "E86", {"start": v(15, 104.25) * mm, "mid": v(0, 119.25) * mm, "end": v(-15, 104.25) * mm});
            skLineSegment(sketch, "E87", {"start": v(-74.44, 0) * mm, "end": v(74.03, 0) * mm, "construction": true});
            skArc(sketch, "E88.MirrorCS", {"start": v(15, -104.25) * mm, "mid": v(0, -119.25) * mm, "end": v(-15, -104.25) * mm});
            skLineSegment(sketch, "E89.MirrorCS", {"start": v(-15, -92.25) * mm, "end": v(-15, -104.25) * mm});
            skLineSegment(sketch, "E90.MirrorCS", {"start": v(15, -92.25) * mm, "end": v(15, -104.25) * mm});
            skLineSegment(sketch, "E91.MirrorCS", {"start": v(33, -74.25) * mm, "end": v(15, -92.25) * mm});
            skLineSegment(sketch, "E92.MirrorCS", {"start": v(-33, -74.25) * mm, "end": v(-15, -92.25) * mm});
            skLineSegment(sketch, "E93.MirrorCS", {"start": v(33, -74.25) * mm, "end": v(-33, -74.25) * mm});
            skCircle(sketch, "E94.MirrorC", {"center": v(0, -104.25) * mm, "radius": 6 * mm});
            skLineSegment(sketch, "E95.MirrorCS", {"start": v(0, -74.25) * mm, "end": v(0, -104.25) * mm, "construction": true});
            skSolve(sketch);
        }
        {
            var Q0;
            Q0 = qSketchRegion(id + "F17", true);
            extrude(context, id + "F18", {"entities" : qUnion([Q0]), "oppositeDirection" : true, "depth" : 25 * mm});
        }
    });
